# Revit family: окна.rehau_бд-однопольное_слева(фрамуга)
name_source: partatom
category: Окна
revit_build: Autodesk Revit 2017 (Build: 20161006_0315(x64)
units: mm (PartAtom-declared; Revit-internal decimal feet)

## family parameters
Всегда вертикально = Да
Заголовок OmniClass = Windows
Номер OmniClass = 23.30.20.00
Общий = Нет
Основа = Стена
При загрузке вырезать с полостями = Нет
Точка расчета площади = Нет

## types (2) — shared parameters
24 газ = сп : однокамерный (24мм) заполнение газом
24 обычный = сп : однокамерный (24мм) обычный
24 энерго = сп : однокамерный (24мм) энергосберегающие стекла
32 газ = сп : двухкамерный (32мм) заполнение газом
32 обычный = сп : двухкамерный (32мм) обычный
32 триплекс = сп : двухкамерный (32мм) триплекс
32 энерго = сп : двухкамерный (32мм) энергосберегающие стекла
ADSK_Обозначение = ГОСТ 30674-99
URL = https://www.rehau.com
blitz new = Rehau : BLITZ NEW
delight 78 = Rehau : DELIGHT
euro 64 = Rehau : EURO (коробка 64, импост 78, створка 60)
euro 68 = Rehau : EURO (коробка 68, импост 78, створка 60)
euro 76 = Rehau : EURO (коробка 76, импост 86, створка 74)
grazio 55 = Rehau : GRAZIO (коробка 55)
grazio 63 = Rehau : GRAZIO (коробка 63)
Аналитическая конструкция = Окна с одинарным остеклением - для жилых зданий
Высота окна = 1460 мм
Высота подоконника по умолчанию = 100 мм
Высота расположения импоста двери = 850 мм
Высота фрамуги = 400 мм
Группа модели = БП
Длина соединителя профилей = 1460 мм
Замыкание стены = По основе
Изготовитель = Rehau
Изображение типоразмера = <Нет>
Коэффициент теплопередачи (U) = 5.7361 Вт/(м²·K)
Коэффициент теплопритока от солнечного излучения = 0.86
Материал коробки = <По категории>
Материал отлива = <По категории>
Материал подоконника = <По категории>
Материал стекла = <По категории>
Описание = проем.окно
Примерная высота = 2360 мм
Примерная ширина = 1560 мм
Пропускание видимого света = 0.9
Термостойкость = 0.1743 (м²·K)/Вт
Тип двери = дверь : без импоста
Тип створки = створка : глухая
Тип фрамуги = створка : глухая
Ширина двери = 680 мм
Ширина окна = 880 мм
бд_без_и_1 = дверь : без импоста
бд_без_и_2 = дверь : без импоста (верхнее открывание)
глухая_створка = створка : глухая
обозначение_проема_высота = 393 мм
обозначение_проема_ширина = 260 мм
таблица выбора = каталог профилей Rehau

## type names (no varying parameters)
- 2360х1560 (левое открывание)
- 2360х1560 (глухое)
